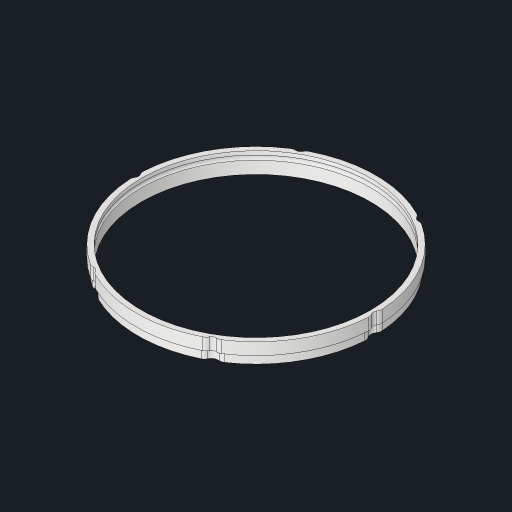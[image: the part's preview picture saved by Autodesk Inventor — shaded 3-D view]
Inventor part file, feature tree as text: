
AUTODESK INVENTOR PART (.ipt)
format: ipt  version: 2023.2 (Build 272271030, 271C)  size: 195,072 bytes
history: native  units: mm
features: sketch x3, extrude x2, revolve x1, fillet x1, pattern_circular x1
ambient origin geometry x8: Origin, YZ Plane, XZ Plane, XY Plane, X Axis, Y Axis, Z Axis, Center Point
bodies: Solid1 (feature_tree)
feature tree (8):
  revolve  "Revolution1"  [1 undecoded]
  extrude  "Extrusion1"  Depth=67.0mm
  extrude  "Extrusion2"  Depth=4.0mm
  fillet  "Fillet1"  Radius=71.25mm
  pattern_circular  "Circular Pattern1"  [2 undecoded]
  sketch  "Sketch1"  dims[d0=5.0mm d1=69.0mm]
  sketch  "Sketch2"  dims[d4=7.0mm d7=67.0mm]
  sketch  "Sketch3"  dims[d15=360.0deg d16=5.1mm d17=71.25mm d18=10.0mm d19=0.0mm d20=8.0mm d21=10.0mm d22=0.0mm d23=4.0mm d24=60.0mm d25=360.0deg d27=4.0mm d28=67.5mm d29=1.0mm]
note: 3 required parameter values undecoded (feature->parameter linkage not recoverable at this tier; creation-order binding heuristic only, values carry confidence <= 0.55)